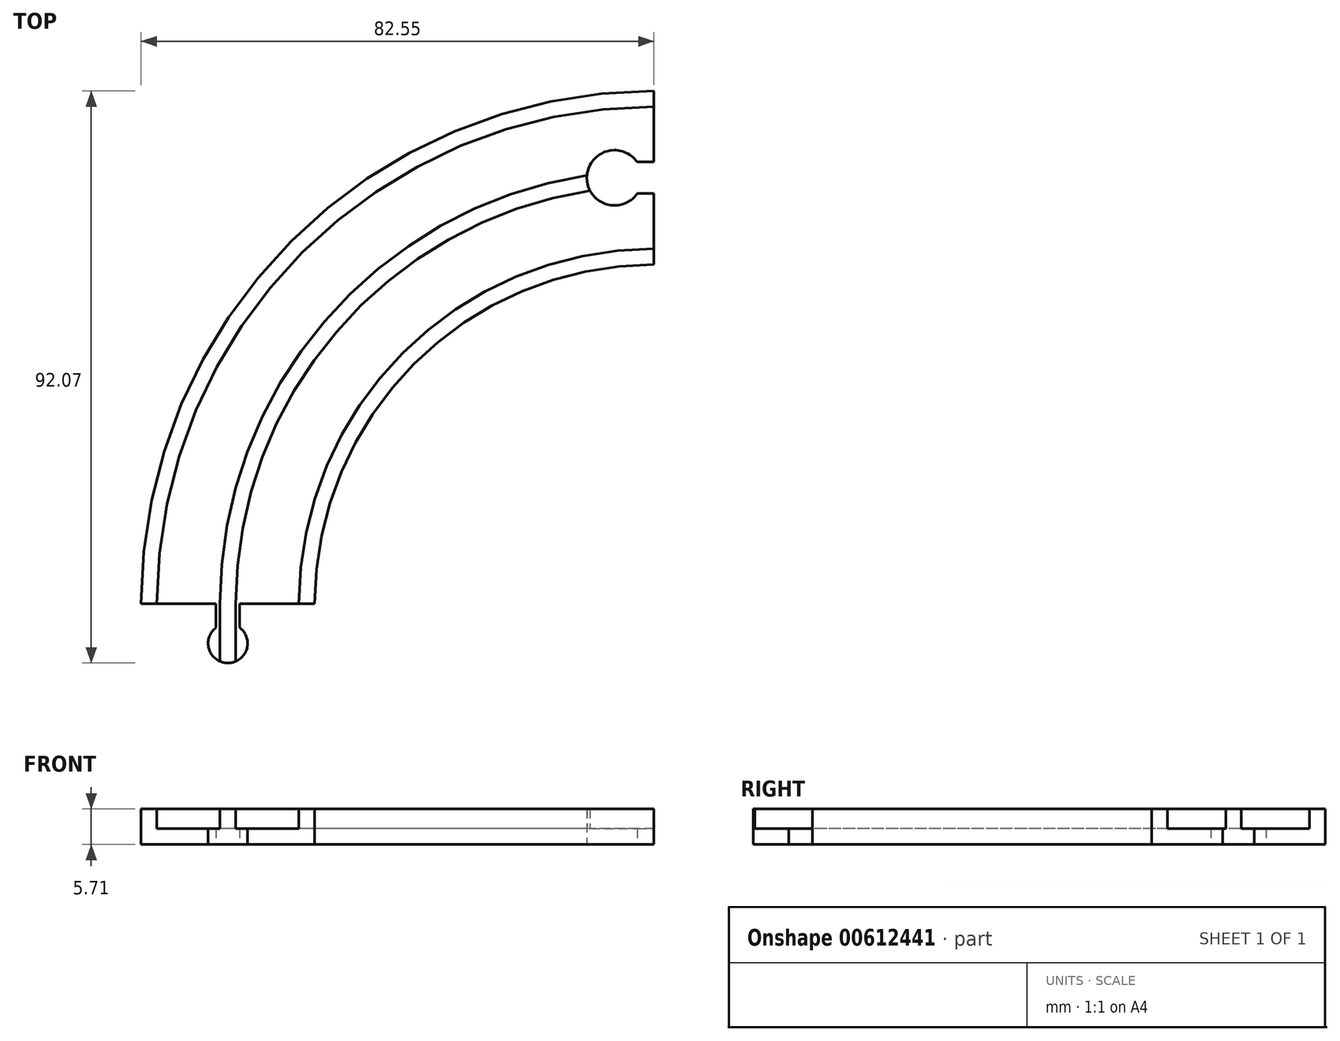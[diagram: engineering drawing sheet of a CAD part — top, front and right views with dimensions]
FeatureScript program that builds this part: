
annotation { "Feature Type Name" : "Feature", "Feature Type Description" : "" }
export const myFeature = defineFeature(function(context is Context, id is Id, definition is map)
    precondition{}
    {
        {
            var Q0;
            Q0=qCreatedBy(makeId("Top.planeOp"),FACE);
            var sketch = newSketch(context, id + "F0", { "sketchPlane" : qUnion([Q0])});
            skLineSegment(sketch, "E0", {"start": v(0, 0) * mm, "end": v(27.94, 0) * mm});
            skLineSegment(sketch, "E1", {"start": v(0, 0) * mm, "end": v(0, 0) * mm});
            skLineSegment(sketch, "E2", {"start": v(82.55, 82.55) * mm, "end": v(82.55, 82.55) * mm});
            skLineSegment(sketch, "E3", {"start": v(82.55, 82.55) * mm, "end": v(82.55, 54.6) * mm});
            skPoint(sketch, "E4.visualSharp", {"position": v(25.4, 54.6) * mm});
            skPoint(sketch, "E5.visualSharp", {"position": v(0, 82.55) * mm});
            skArc(sketch, "E5.filletArc", {"start": v(82.55, 82.55) * mm, "mid": v(24.18, 58.37) * mm, "end": v(0, 0) * mm});
            skArc(sketch, "E6.0", {"start": v(82.55, 54.61) * mm, "mid": v(43.93, 38.62) * mm, "end": v(27.94, 0) * mm});
            skSolve(sketch);
        }
        {
            var Q0;
            Q0 = qSketchRegion(id + "F0", true);
            extrude(context, id + "F1", {"entities" : qUnion([Q0]), "depth" : 2.54 * mm, "offsetDistance" : 25.4 * mm});
        }
        {
            var Q0;
            Q0=makeQuery(id+"F1.opExtrude","CAP_FACE",FACE,{"disambiguationData":[OSD([sQuery(id+"F0.wireOp",EDGE,"E0"),sQuery(id+"F0.wireOp",EDGE,"E3"),sQuery(id+"F0.wireOp",EDGE,"E5.filletArc"),sQuery(id+"F0.wireOp",EDGE,"E6.0")])],"isStart":false});
            var sketch = newSketch(context, id + "F2", { "sketchPlane" : qUnion([Q0])});
            skArc(sketch, "E7.0", {"start": v(82.55, 82.55) * mm, "mid": v(24.18, 58.37) * mm, "end": v(0, 0) * mm});
            skArc(sketch, "E8.0", {"start": v(82.55, 80.01) * mm, "mid": v(25.97, 56.58) * mm, "end": v(2.54, 0) * mm});
            skArc(sketch, "E9.0", {"start": v(82.55, 57.15) * mm, "mid": v(42.14, 40.41) * mm, "end": v(25.4, 0) * mm});
            skArc(sketch, "E10.0", {"start": v(82.55, 54.61) * mm, "mid": v(43.93, 38.62) * mm, "end": v(27.94, 0) * mm});
            skLineSegment(sketch, "E11", {"start": v(2.54, 0) * mm, "end": v(0, 0) * mm});
            skLineSegment(sketch, "E12", {"start": v(27.94, 0) * mm, "end": v(25.4, 0) * mm});
            skLineSegment(sketch, "E13", {"start": v(82.55, 82.55) * mm, "end": v(82.55, 80.01) * mm});
            skLineSegment(sketch, "E14", {"start": v(82.55, 57.15) * mm, "end": v(82.55, 54.61) * mm});
            skArc(sketch, "E15.0", {"start": v(82.55, 68.58) * mm, "mid": v(34.06, 48.5) * mm, "end": v(13.97, 0) * mm, "construction": true});
            skArc(sketch, "E16", {"start": v(82.55, 69.85) * mm, "mid": v(33.16, 49.4) * mm, "end": v(12.7, 0) * mm});
            skArc(sketch, "E17", {"start": v(82.55, 67.31) * mm, "mid": v(34.95, 47.6) * mm, "end": v(15.24, 0) * mm});
            skLineSegment(sketch, "E18", {"start": v(12.7, 0) * mm, "end": v(15.24, 0) * mm});
            skLineSegment(sketch, "E19", {"start": v(82.55, 67.31) * mm, "end": v(82.55, 69.85) * mm});
            skSolve(sketch);
        }
        {
            var Q0;
            Q0 = qSketchRegion(id + "F2", true);
            extrude(context, id + "F3", {"entities" : qUnion([Q0]), "operationType" : NewBodyOperationType.ADD, "depth" : 3.17 * mm, "offsetDistance" : 25.4 * mm});
        }
        {
            var Q0;
            Q0=makeQuery(id+"F1.opExtrude","CAP_FACE",FACE,{"disambiguationData":[OSD([sQuery(id+"F0.wireOp",EDGE,"E0"),sQuery(id+"F0.wireOp",EDGE,"E3"),sQuery(id+"F0.wireOp",EDGE,"E5.filletArc"),sQuery(id+"F0.wireOp",EDGE,"E6.0")])],"isStart":true});
            var sketch = newSketch(context, id + "F4", { "sketchPlane" : qUnion([Q0])});
            skLineSegment(sketch, "E20", {"start": v(13.97, 0) * mm, "end": v(13.97, 3.6) * mm, "construction": true});
            skPoint(sketch, "E20.endSnap0", {"position": v(13.97, 0) * mm});
            skLineSegment(sketch, "E21", {"start": v(12.07, 0) * mm, "end": v(12.07, 3.81) * mm});
            skLineSegment(sketch, "E22", {"start": v(15.88, 0) * mm, "end": v(15.88, 3.81) * mm});
            skArc(sketch, "E23", {"start": v(15.88, 3.81) * mm, "mid": v(13.97, 9.53) * mm, "end": v(12.07, 3.81) * mm});
            skPoint(sketch, "E23.third.point", {"position": v(13.97, 9.53) * mm});
            skSolve(sketch);
        }
        {
            var Q0;
            {var subQ0=sQuery(id+"F4.wireOp",EDGE,"E21");Q0=makeQuery(id+"F4.imprint","IMPRINT",FACE,{"disambiguationData":[TD([[makeQuery(id+"F4.imprint","IMPRINT",EDGE,{"derivedFrom":subQ0}),-1.0]])]});}
            var Q1;
            {var subQ0=sQuery(id+"F0.wireOp",EDGE,"E3");var subQ1=sQuery(id+"F0.wireOp",EDGE,"E0");Q1=makeQuery(id+"F3.boolean.opBoolean","SPLIT",FACE,{"disambiguationData":[TD([makeQuery(id+"F3.opExtrude","SWEPT_FACE",FACE,{"disambiguationData":[OSD([sQuery(id+"F2.wireOp",EDGE,"E9.0")])]})])],"derivedFrom":makeQuery(id+"F1.opExtrude","CAP_FACE",FACE,{"disambiguationData":[OSD([subQ1,subQ0,sQuery(id+"F0.wireOp",EDGE,"E5.filletArc"),sQuery(id+"F0.wireOp",EDGE,"E6.0")])],"isStart":false})});}
            extrude(context, id + "F5", {"entities" : qUnion([Q0]), "operationType" : NewBodyOperationType.ADD, "endBound" : BoundingType.UP_TO_SURFACE, "oppositeDirection" : true, "depth" : 25.4 * mm, "endBoundEntityFace" : qUnion([Q1]), "offsetDistance" : 25.4 * mm});
        }
        {
            var Q0;
            {var subQ0=sQuery(id+"F0.wireOp",EDGE,"E0");Q0=makeQuery(id+"F5.boolean.opBoolean","MERGE",FACE,{"derivedFrom":[makeQuery(id+"F1.opExtrude","CAP_FACE",FACE,{"disambiguationData":[OSD([subQ0,sQuery(id+"F0.wireOp",EDGE,"E3"),sQuery(id+"F0.wireOp",EDGE,"E5.filletArc"),sQuery(id+"F0.wireOp",EDGE,"E6.0")])],"isStart":true}),makeQuery(id+"F5.opExtrude","CAP_FACE",FACE,{"disambiguationData":[OSD([subQ0,sQuery(id+"F4.wireOp",EDGE,"E21"),sQuery(id+"F4.wireOp",EDGE,"E22"),sQuery(id+"F4.wireOp",EDGE,"E23")])],"isStart":true})]});}
            var sketch = newSketch(context, id + "F6", { "sketchPlane" : qUnion([Q0])});
            skLineSegment(sketch, "E24", {"start": v(82.55, -68.58) * mm, "end": v(80.33, -68.58) * mm, "construction": true});
            skPoint(sketch, "E24.endSnap0", {"position": v(82.55, -68.58) * mm});
            skLineSegment(sketch, "E25", {"start": v(82.55, -66.04) * mm, "end": v(79.85, -66.04) * mm});
            skLineSegment(sketch, "E26.MirrorCS", {"start": v(82.55, -71.12) * mm, "end": v(79.85, -71.12) * mm});
            skArc(sketch, "E27", {"start": v(79.85, -66.04) * mm, "mid": v(71.76, -68.58) * mm, "end": v(79.85, -71.12) * mm});
            skPoint(sketch, "E27.third.point", {"position": v(71.76, -68.8) * mm});
            skSolve(sketch);
        }
        {
            var Q0;
            {var subQ0=sQuery(id+"F6.wireOp",EDGE,"E25");Q0=makeQuery(id+"F6.imprint","IMPRINT",FACE,{"disambiguationData":[TD([[makeQuery(id+"F6.imprint","IMPRINT",EDGE,{"derivedFrom":subQ0}),1.0]])]});}
            extrude(context, id + "F7", {"entities" : qUnion([Q0]), "operationType" : NewBodyOperationType.REMOVE, "oppositeDirection" : true, "depth" : 25.4 * mm, "offsetDistance" : 25.4 * mm});
        }
        {
            var Q0;
            {var subQ2=sQuery(id+"F0.wireOp",EDGE,"E0");var subQ3=sQuery(id+"F2.wireOp",EDGE,"E17");var subQ4=sQuery(id+"F2.wireOp",EDGE,"E18");var subQ5=makeQuery(id+"F3.opExtrude","SWEPT_FACE",FACE,{"disambiguationData":[OSD([subQ4])]});var subQ6=sQuery(id+"F2.wireOp",EDGE,"E16");var subQ7=makeQuery(id+"F1.opExtrude","SWEPT_FACE",FACE,{"disambiguationData":[OSD([subQ2])]});var subQ8=makeQuery(id+"F3.opExtrude","SWEPT_FACE",FACE,{"disambiguationData":[OSD([sQuery(id+"F2.wireOp",EDGE,"E12")])]});var subQ9=makeQuery(id+"F3.opExtrude","SWEPT_FACE",FACE,{"disambiguationData":[OSD([sQuery(id+"F2.wireOp",EDGE,"E11")])]});Q0=makeQuery(id+"F5.boolean.opBoolean","SPLIT",FACE,{"disambiguationData":[TD([makeQuery(id+"F3.opExtrude","CAP_FACE",FACE,{"disambiguationData":[OSD([subQ6,subQ3,subQ4,sQuery(id+"F2.wireOp",EDGE,"E19")])],"isStart":false})])],"derivedFrom":makeQuery(id+"F3.boolean.opBoolean","MERGE",FACE,{"derivedFrom":[subQ7,subQ9,subQ8,subQ5]})});}
            var sketch = newSketch(context, id + "F8", { "sketchPlane" : qUnion([Q0])});
            skLineSegment(sketch, "E28.bottom", {"start": v(12.7, 5.72) * mm, "end": v(15.24, 5.72) * mm});
            skLineSegment(sketch, "E28.top", {"start": v(12.7, 2.54) * mm, "end": v(15.24, 2.54) * mm});
            skLineSegment(sketch, "E28.left", {"start": v(12.7, 5.72) * mm, "end": v(12.7, 2.54) * mm});
            skLineSegment(sketch, "E28.right", {"start": v(15.24, 5.72) * mm, "end": v(15.24, 2.54) * mm});
            skSolve(sketch);
        }
        {
            var Q0;
            Q0 = qSketchRegion(id + "F8", true);
            extrude(context, id + "F9", {"entities" : qUnion([Q0]), "operationType" : NewBodyOperationType.ADD, "depth" : 10.16 * mm, "offsetDistance" : 25.4 * mm});
        }
        {
            var Q0;
            {var subQ0=sQuery(id+"F0.wireOp",EDGE,"E0");Q0=makeQuery(id+"F5.boolean.opBoolean","MERGE",FACE,{"derivedFrom":[makeQuery(id+"F1.opExtrude","CAP_FACE",FACE,{"disambiguationData":[OSD([subQ0,sQuery(id+"F0.wireOp",EDGE,"E3"),sQuery(id+"F0.wireOp",EDGE,"E5.filletArc"),sQuery(id+"F0.wireOp",EDGE,"E6.0")])],"isStart":true}),makeQuery(id+"F5.opExtrude","CAP_FACE",FACE,{"disambiguationData":[OSD([subQ0,sQuery(id+"F4.wireOp",EDGE,"E21"),sQuery(id+"F4.wireOp",EDGE,"E22"),sQuery(id+"F4.wireOp",EDGE,"E23")])],"isStart":true})]});}
            var sketch = newSketch(context, id + "F10", { "sketchPlane" : qUnion([Q0])});
            skArc(sketch, "E29", {"start": v(17.15, 6.35) * mm, "mid": v(13.97, 9.53) * mm, "end": v(10.8, 6.35) * mm});
            skPoint(sketch, "E29.first.point", {"position": v(10.85, 6.93) * mm});
            skPoint(sketch, "E29.second.point", {"position": v(17.12, 5.93) * mm});
            skPoint(sketch, "E29.third.point", {"position": v(13.97, 9.53) * mm});
            skLineSegment(sketch, "E30", {"start": v(10.8, 6.35) * mm, "end": v(10.8, 10.75) * mm});
            skLineSegment(sketch, "E31", {"start": v(10.8, 10.75) * mm, "end": v(17.15, 10.75) * mm});
            skLineSegment(sketch, "E32", {"start": v(17.15, 10.75) * mm, "end": v(17.15, 6.35) * mm});
            skSolve(sketch);
        }
        {
            var Q0;
            Q0=makeQuery(id+"F10.imprint","IMPRINT",FACE,{"disambiguationData":[TD([[makeQuery(id+"F10.imprint","IMPRINT",EDGE,{"derivedFrom":sQuery(id+"F10.wireOp",EDGE,"E29")}),-1.0]])]});
            extrude(context, id + "F11", {"entities" : qUnion([Q0]), "operationType" : NewBodyOperationType.REMOVE, "oppositeDirection" : true, "depth" : 25.4 * mm, "offsetDistance" : 25.4 * mm});
        }
    });
